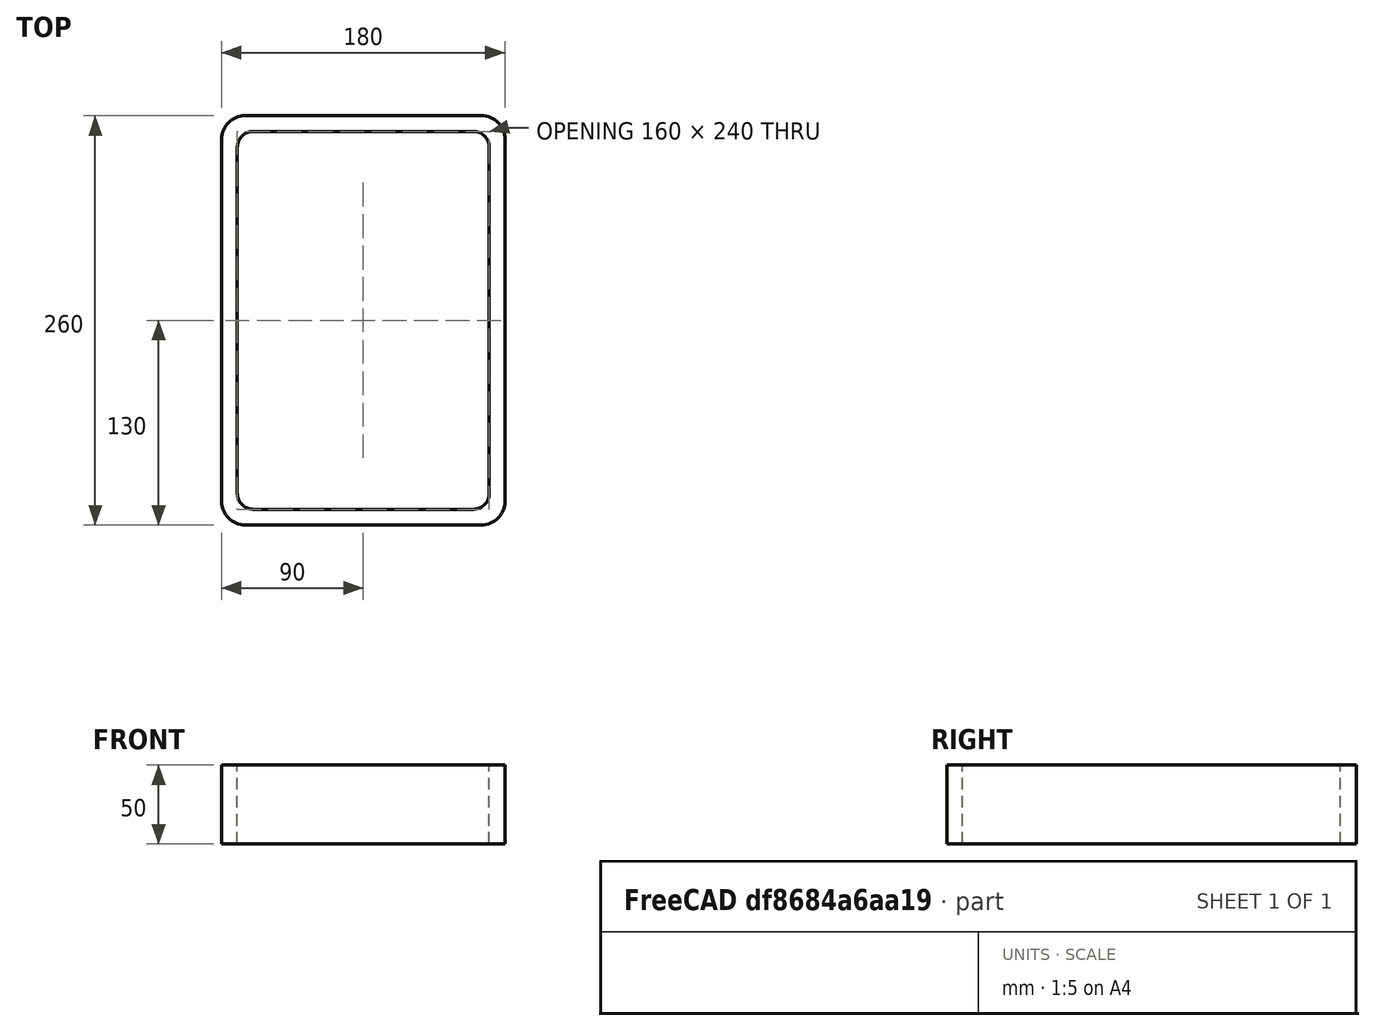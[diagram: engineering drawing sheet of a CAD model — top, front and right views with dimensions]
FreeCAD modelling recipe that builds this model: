
FCSTD DOCUMENT  (FreeCAD 0.15R4671 (Git))
Label: Rectangular hollow section 260x180x10 EN10219 S235JRH
License: All rights reserved
LicenseURL: http://en.wikipedia.org/wiki/All_rights_reserved
objects: Sketcher::SketchObject×1, Part::Extrusion×1
note: 2 computed .brp shape members not serialized (recipe doc carries the construction recipe); baked Part::Feature solids carry a one-line shape summary decoded from their .brp

FEATURE [Sketcher::SketchObject] Sketch
  sketch-geometry (16):
    g0: LineSegment StartX=-70 StartY=120 StartZ=0 EndX=70 EndY=120 EndZ=0
    g1: LineSegment StartX=80 StartY=110 StartZ=0 EndX=80 EndY=-110 EndZ=0
    g2: LineSegment StartX=70 StartY=-120 StartZ=0 EndX=-70 EndY=-120 EndZ=0
    g3: LineSegment StartX=-80 StartY=-110 StartZ=0 EndX=-80 EndY=110 EndZ=0
    g4: LineSegment StartX=-75 StartY=130 StartZ=0 EndX=75 EndY=130 EndZ=0
    g5: LineSegment StartX=90 StartY=115 StartZ=0 EndX=90 EndY=-115 EndZ=0
    g6: LineSegment StartX=75 StartY=-130 StartZ=0 EndX=-75 EndY=-130 EndZ=0
    g7: LineSegment StartX=-90 StartY=-115 StartZ=0 EndX=-90 EndY=115 EndZ=0
    g8: ArcOfCircle CenterX=-70 CenterY=110 CenterZ=0 NormalX=0 NormalY=0 NormalZ=1 Radius=10 StartAngle=1.5708 EndAngle=3.14159
    g9: ArcOfCircle CenterX=70 CenterY=110 CenterZ=0 NormalX=0 NormalY=0 NormalZ=1 Radius=10 StartAngle=0 EndAngle=1.5708
    g10: ArcOfCircle CenterX=70 CenterY=-110 CenterZ=0 NormalX=0 NormalY=0 NormalZ=1 Radius=10 StartAngle=4.71239 EndAngle=6.28319
    g11: ArcOfCircle CenterX=-70 CenterY=-110 CenterZ=0 NormalX=0 NormalY=0 NormalZ=1 Radius=10 StartAngle=3.14159 EndAngle=4.71239
    g12: ArcOfCircle CenterX=75 CenterY=115 CenterZ=0 NormalX=0 NormalY=0 NormalZ=1 Radius=15 StartAngle=0 EndAngle=1.5708
    g13: ArcOfCircle CenterX=75 CenterY=-115 CenterZ=0 NormalX=0 NormalY=0 NormalZ=1 Radius=15 StartAngle=4.71239 EndAngle=6.28319
    g14: ArcOfCircle CenterX=-75 CenterY=-115 CenterZ=0 NormalX=0 NormalY=0 NormalZ=1 Radius=15 StartAngle=3.14159 EndAngle=4.71239
    g15: ArcOfCircle CenterX=-75 CenterY=115 CenterZ=0 NormalX=0 NormalY=0 NormalZ=1 Radius=15 StartAngle=1.5708 EndAngle=3.14159
  constraints (36):
    c: Horizontal(g2)
    c: Vertical(g3)
    c: Horizontal(g6)
    c: Vertical(g7)
    c: Tangent(g3,g8) = 1.5708
    c: Tangent(g0,g8) = 1.5708
    c: Tangent(g0,g9) = 1.5708
    c: Tangent(g1,g9) = 1.5708
    c: Tangent(g1,g10) = 1.5708
    c: Tangent(g2,g10) = 1.5708
    c: Tangent(g2,g11) = 1.5708
    c: Tangent(g3,g11) = 1.5708
    c: Tangent(g4,g12) = 1.5708
    c: Tangent(g5,g12) = 1.5708
    c: Tangent(g5,g13) = 1.5708
    c: Tangent(g6,g13) = 1.5708
    c: Tangent(g6,g14) = 1.5708
    c: Tangent(g7,g14) = 1.5708
    c: Tangent(g7,g15) = 1.5708
    c: Tangent(g4,g15) = 1.5708
    c: Equal(g9,g8)
    c: Equal(g9,g11)
    c: Equal(g9,g10)
    c: Equal(g12,g15)
    c: Equal(g12,g14)
    c: Equal(g12,g13)
    c: Symmetric(g4,g6,g-1)
    c: Symmetric(g7,g5,g-2)
    c: DistanceY(g4,g6) = -260
    c: DistanceX(g7,g5) = 180
    c: Symmetric(g3,g1,g-2)
    c: Symmetric(g0,g2,g-1)
    c: DistanceY(g0,g4) = 10
    c: DistanceX(g5,g1) = -10
    c: Radius(g9) = 10
    c: Radius(g12) = 15
FEATURE [Part::Extrusion] Extrude  label="Rectangular hollow section 260x180x10 EN10219 S235JRH"
  Base = -> Sketch
  Dir = (0,0,50)
  Solid = true
